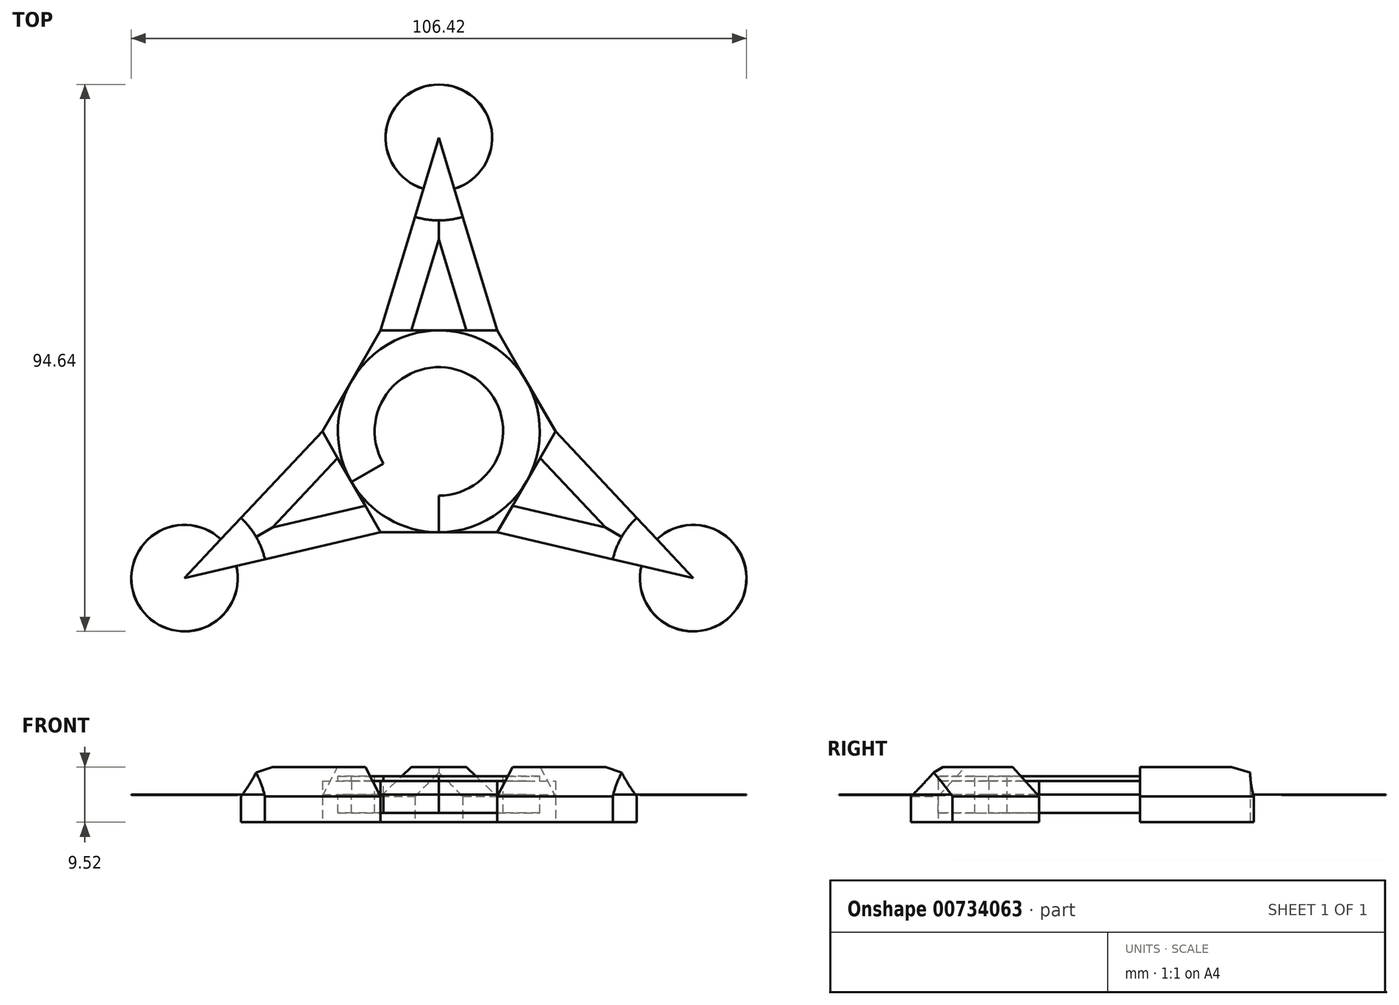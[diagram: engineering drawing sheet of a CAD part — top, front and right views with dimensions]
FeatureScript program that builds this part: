
annotation { "Feature Type Name" : "Feature", "Feature Type Description" : "" }
export const myFeature = defineFeature(function(context is Context, id is Id, definition is map)
    precondition{}
    {
        {
            var Q0;
            Q0=qCreatedBy(makeId("Top.planeOp"),FACE);
            var sketch = newSketch(context, id + "F0", { "sketchPlane" : qUnion([Q0])});
            skCircle(sketch, "E0", {"center": v(0, 0) * mm, "radius": 11.11 * mm});
            skCircle(sketch, "E1", {"center": v(0, 0) * mm, "radius": 17.46 * mm});
            skPoint(sketch, "E2.0.midPoint", {"position": v(15.12, 8.73) * mm});
            skCircle(sketch, "E3.cCircle", {"center": v(0, 0) * mm, "radius": 17.46 * mm, "construction": true});
            skLineSegment(sketch, "E3.0", {"start": v(10.08, 17.46) * mm, "end": v(20.16, 0) * mm});
            skLineSegment(sketch, "E3.1", {"start": v(20.16, 0) * mm, "end": v(10.08, -17.46) * mm});
            skLineSegment(sketch, "E3.2", {"start": v(10.08, -17.46) * mm, "end": v(-10.08, -17.46) * mm});
            skLineSegment(sketch, "E3.3", {"start": v(-10.08, -17.46) * mm, "end": v(-20.16, 0) * mm});
            skLineSegment(sketch, "E3.4", {"start": v(-20.16, 0) * mm, "end": v(-10.08, 17.46) * mm});
            skLineSegment(sketch, "E3.5", {"start": v(-10.08, 17.46) * mm, "end": v(10.08, 17.46) * mm});
            skLineSegment(sketch, "E4", {"start": v(-10.08, 17.46) * mm, "end": v(0, 50.8) * mm});
            skLineSegment(sketch, "E5", {"start": v(0, 50.8) * mm, "end": v(10.08, 17.46) * mm});
            skLineSegment(sketch, "E6", {"start": v(0, 50.8) * mm, "end": v(0, -50.8) * mm});
            skLineSegment(sketch, "E7", {"start": v(-20.16, 0) * mm, "end": v(-44, -25.4) * mm});
            skLineSegment(sketch, "E8", {"start": v(-44, -25.4) * mm, "end": v(-10.08, -17.46) * mm});
            skLineSegment(sketch, "E9", {"start": v(-44, -25.4) * mm, "end": v(44, 25.4) * mm});
            skLineSegment(sketch, "E10", {"start": v(10.08, -17.46) * mm, "end": v(44, -25.4) * mm});
            skLineSegment(sketch, "E11", {"start": v(44, -25.4) * mm, "end": v(20.16, 0) * mm});
            skLineSegment(sketch, "E12", {"start": v(44, -25.4) * mm, "end": v(-44, 25.4) * mm});
            skCircle(sketch, "E13", {"center": v(-44, -25.4) * mm, "radius": 14.29 * mm});
            skCircle(sketch, "E14", {"center": v(44, -25.4) * mm, "radius": 14.29 * mm});
            skCircle(sketch, "E15", {"center": v(0, 50.8) * mm, "radius": 14.29 * mm});
            skSolve(sketch);
        }
        {
            var Q0;
            {var subQ0=sQuery(id+"F0.wireOp",EDGE,"E9");var subQ1=sQuery(id+"F0.wireOp",EDGE,"E0");var subQ2=makeQuery(id+"F0.imprint","INTERSECT",VERTEX,{"disambiguationData":[OD(1.0)],"derivedFrom":[subQ1,subQ0]});Q0=makeQuery(id+"F0.imprint","IMPRINT",FACE,{"disambiguationData":[TD([[makeQuery(id+"F0.imprint","IMPRINT",EDGE,{"disambiguationData":[TD([[subQ2,-1.0]])],"derivedFrom":subQ1}),-1.0]])]});}
            var Q1;
            {var subQ0=sQuery(id+"F0.wireOp",EDGE,"E6");var subQ1=sQuery(id+"F0.wireOp",EDGE,"E0");var subQ2=makeQuery(id+"F0.imprint","INTERSECT",VERTEX,{"disambiguationData":[OD(0.0)],"derivedFrom":[subQ1,subQ0]});Q1=makeQuery(id+"F0.imprint","IMPRINT",FACE,{"disambiguationData":[TD([[makeQuery(id+"F0.imprint","IMPRINT",EDGE,{"disambiguationData":[TD([[subQ2,-1.0]])],"derivedFrom":subQ1}),-1.0]])]});}
            var Q2;
            {var subQ0=sQuery(id+"F0.wireOp",EDGE,"E12");var subQ1=sQuery(id+"F0.wireOp",EDGE,"E0");var subQ2=makeQuery(id+"F0.imprint","INTERSECT",VERTEX,{"disambiguationData":[OD(0.0)],"derivedFrom":[subQ1,subQ0]});Q2=makeQuery(id+"F0.imprint","IMPRINT",FACE,{"disambiguationData":[TD([[makeQuery(id+"F0.imprint","IMPRINT",EDGE,{"disambiguationData":[TD([[subQ2,-1.0]])],"derivedFrom":subQ1}),-1.0]])]});}
            var Q3;
            {var subQ0=sQuery(id+"F0.wireOp",EDGE,"E6");var subQ1=sQuery(id+"F0.wireOp",EDGE,"E0");var subQ2=makeQuery(id+"F0.imprint","INTERSECT",VERTEX,{"disambiguationData":[OD(0.0)],"derivedFrom":[subQ1,subQ0]});Q3=makeQuery(id+"F0.imprint","IMPRINT",FACE,{"disambiguationData":[TD([[makeQuery(id+"F0.imprint","IMPRINT",EDGE,{"disambiguationData":[TD([[subQ2,1.0]])],"derivedFrom":subQ1}),-1.0]])]});}
            var Q4;
            {var subQ0=sQuery(id+"F0.wireOp",EDGE,"E9");var subQ1=sQuery(id+"F0.wireOp",EDGE,"E0");var subQ2=makeQuery(id+"F0.imprint","INTERSECT",VERTEX,{"disambiguationData":[OD(0.0)],"derivedFrom":[subQ1,subQ0]});Q4=makeQuery(id+"F0.imprint","IMPRINT",FACE,{"disambiguationData":[TD([[makeQuery(id+"F0.imprint","IMPRINT",EDGE,{"disambiguationData":[TD([[subQ2,1.0]])],"derivedFrom":subQ1}),-1.0]])]});}
            var Q5;
            {var subQ0=sQuery(id+"F0.wireOp",EDGE,"E6");var subQ1=sQuery(id+"F0.wireOp",EDGE,"E0");var subQ2=makeQuery(id+"F0.imprint","INTERSECT",VERTEX,{"disambiguationData":[OD(1.0)],"derivedFrom":[subQ1,subQ0]});Q5=makeQuery(id+"F0.imprint","IMPRINT",FACE,{"disambiguationData":[TD([[makeQuery(id+"F0.imprint","IMPRINT",EDGE,{"disambiguationData":[TD([[subQ2,-1.0]])],"derivedFrom":subQ1}),-1.0]])]});}
            extrude(context, id + "F1", {"entities" : qUnion([Q0, Q1, Q2, Q3, Q4, Q5]), "oppositeDirection" : true, "depth" : 3.17 * mm, "offsetDistance" : 25.4 * mm, "hasSecondDirection" : true, "secondDirectionOppositeDirection" : false, "secondDirectionDepth" : 3.17 * mm});
        }
        {
            var Q0;
            {var subQ0=sQuery(id+"F0.wireOp",EDGE,"E3.4");var subQ1=sQuery(id+"F0.wireOp",EDGE,"E1");var subQ2=makeQuery(id+"F0.imprint","INTERSECT",VERTEX,{"derivedFrom":[subQ1,subQ0,sQuery(id+"F0.wireOp",EDGE,"E12")]});Q0=makeQuery(id+"F0.imprint","IMPRINT",FACE,{"disambiguationData":[TD([[makeQuery(id+"F0.imprint","IMPRINT",EDGE,{"disambiguationData":[TD([[subQ2,-1.0]])],"derivedFrom":subQ1}),-1.0]])]});}
            var Q1;
            {var subQ0=sQuery(id+"F0.wireOp",EDGE,"E3.2");var subQ1=sQuery(id+"F0.wireOp",EDGE,"E1");var subQ2=makeQuery(id+"F0.imprint","INTERSECT",VERTEX,{"derivedFrom":[subQ1,subQ0,sQuery(id+"F0.wireOp",EDGE,"E6")]});Q1=makeQuery(id+"F0.imprint","IMPRINT",FACE,{"disambiguationData":[TD([[makeQuery(id+"F0.imprint","IMPRINT",EDGE,{"disambiguationData":[TD([[subQ2,1.0]])],"derivedFrom":subQ1}),-1.0]])]});}
            var Q2;
            {var subQ0=sQuery(id+"F0.wireOp",EDGE,"E3.4");var subQ1=sQuery(id+"F0.wireOp",EDGE,"E1");var subQ2=makeQuery(id+"F0.imprint","INTERSECT",VERTEX,{"derivedFrom":[subQ1,subQ0,sQuery(id+"F0.wireOp",EDGE,"E12")]});Q2=makeQuery(id+"F0.imprint","IMPRINT",FACE,{"disambiguationData":[TD([[makeQuery(id+"F0.imprint","IMPRINT",EDGE,{"disambiguationData":[TD([[subQ2,1.0]])],"derivedFrom":subQ1}),-1.0]])]});}
            var Q3;
            {var subQ0=sQuery(id+"F0.wireOp",EDGE,"E3.0");var subQ1=sQuery(id+"F0.wireOp",EDGE,"E1");var subQ2=makeQuery(id+"F0.imprint","INTERSECT",VERTEX,{"derivedFrom":[subQ1,subQ0,sQuery(id+"F0.wireOp",EDGE,"E9")]});Q3=makeQuery(id+"F0.imprint","IMPRINT",FACE,{"disambiguationData":[TD([[makeQuery(id+"F0.imprint","IMPRINT",EDGE,{"disambiguationData":[TD([[subQ2,-1.0]])],"derivedFrom":subQ1}),-1.0]])]});}
            var Q4;
            {var subQ0=sQuery(id+"F0.wireOp",EDGE,"E3.2");var subQ1=sQuery(id+"F0.wireOp",EDGE,"E1");var subQ2=makeQuery(id+"F0.imprint","INTERSECT",VERTEX,{"derivedFrom":[subQ1,subQ0,sQuery(id+"F0.wireOp",EDGE,"E6")]});Q4=makeQuery(id+"F0.imprint","IMPRINT",FACE,{"disambiguationData":[TD([[makeQuery(id+"F0.imprint","IMPRINT",EDGE,{"disambiguationData":[TD([[subQ2,-1.0]])],"derivedFrom":subQ1}),-1.0]])]});}
            var Q5;
            {var subQ0=sQuery(id+"F0.wireOp",EDGE,"E3.0");var subQ1=sQuery(id+"F0.wireOp",EDGE,"E1");var subQ2=makeQuery(id+"F0.imprint","INTERSECT",VERTEX,{"derivedFrom":[subQ1,subQ0,sQuery(id+"F0.wireOp",EDGE,"E9")]});Q5=makeQuery(id+"F0.imprint","IMPRINT",FACE,{"disambiguationData":[TD([[makeQuery(id+"F0.imprint","IMPRINT",EDGE,{"disambiguationData":[TD([[subQ2,1.0]])],"derivedFrom":subQ1}),-1.0]])]});}
            extrude(context, id + "F2", {"entities" : qUnion([Q0, Q1, Q2, Q3, Q4, Q5]), "operationType" : NewBodyOperationType.ADD, "depth" : 2.38 * mm, "offsetDistance" : 25.4 * mm, "hasSecondDirection" : true, "secondDirectionOppositeDirection" : true, "secondDirectionDepth" : 3 / 812.8 * mm});
        }
        {
            var Q0;
            {var subQ0=sQuery(id+"F0.wireOp",EDGE,"E10");var subQ5=sQuery(id+"F0.wireOp",EDGE,"E14");var subQ6=makeQuery(id+"F0.imprint","INTERSECT",VERTEX,{"derivedFrom":[subQ0,subQ5]});Q0=makeQuery(id+"F0.imprint","IMPRINT",FACE,{"disambiguationData":[TD([[makeQuery(id+"F0.imprint","IMPRINT",EDGE,{"disambiguationData":[TD([[subQ6,1.0]])],"derivedFrom":subQ5}),-1.0]])]});}
            var Q1;
            {var subQ0=sQuery(id+"F0.wireOp",EDGE,"E11");var subQ5=sQuery(id+"F0.wireOp",EDGE,"E14");var subQ7=makeQuery(id+"F0.imprint","INTERSECT",VERTEX,{"derivedFrom":[subQ0,subQ5]});Q1=makeQuery(id+"F0.imprint","IMPRINT",FACE,{"disambiguationData":[TD([[makeQuery(id+"F0.imprint","IMPRINT",EDGE,{"disambiguationData":[TD([[subQ7,-1.0]])],"derivedFrom":subQ5}),-1.0]])]});}
            var Q2;
            {var subQ0=sQuery(id+"F0.wireOp",EDGE,"E5");var subQ5=sQuery(id+"F0.wireOp",EDGE,"E15");var subQ6=makeQuery(id+"F0.imprint","INTERSECT",VERTEX,{"derivedFrom":[subQ0,subQ5]});Q2=makeQuery(id+"F0.imprint","IMPRINT",FACE,{"disambiguationData":[TD([[makeQuery(id+"F0.imprint","IMPRINT",EDGE,{"disambiguationData":[TD([[subQ6,1.0]])],"derivedFrom":subQ5}),-1.0]])]});}
            var Q3;
            {var subQ0=sQuery(id+"F0.wireOp",EDGE,"E4");var subQ5=sQuery(id+"F0.wireOp",EDGE,"E15");var subQ6=makeQuery(id+"F0.imprint","INTERSECT",VERTEX,{"derivedFrom":[subQ0,subQ5]});Q3=makeQuery(id+"F0.imprint","IMPRINT",FACE,{"disambiguationData":[TD([[makeQuery(id+"F0.imprint","IMPRINT",EDGE,{"disambiguationData":[TD([[subQ6,-1.0]])],"derivedFrom":subQ5}),-1.0]])]});}
            var Q4;
            {var subQ0=sQuery(id+"F0.wireOp",EDGE,"E8");var subQ5=sQuery(id+"F0.wireOp",EDGE,"E13");var subQ6=makeQuery(id+"F0.imprint","INTERSECT",VERTEX,{"derivedFrom":[subQ0,subQ5]});Q4=makeQuery(id+"F0.imprint","IMPRINT",FACE,{"disambiguationData":[TD([[makeQuery(id+"F0.imprint","IMPRINT",EDGE,{"disambiguationData":[TD([[subQ6,-1.0]])],"derivedFrom":subQ5}),-1.0]])]});}
            var Q5;
            {var subQ0=sQuery(id+"F0.wireOp",EDGE,"E7");var subQ5=sQuery(id+"F0.wireOp",EDGE,"E13");var subQ6=makeQuery(id+"F0.imprint","INTERSECT",VERTEX,{"derivedFrom":[subQ0,subQ5]});Q5=makeQuery(id+"F0.imprint","IMPRINT",FACE,{"disambiguationData":[TD([[makeQuery(id+"F0.imprint","IMPRINT",EDGE,{"disambiguationData":[TD([[subQ6,1.0]])],"derivedFrom":subQ5}),-1.0]])]});}
            extrude(context, id + "F3", {"entities" : qUnion([Q0, Q1, Q2, Q3, Q4, Q5]), "surfaceOperationType" : NewSurfaceOperationType.ADD, "depth" : 4.76 * mm, "offsetDistance" : 25.4 * mm, "hasSecondDirection" : true, "secondDirectionOppositeDirection" : true, "secondDirectionDepth" : 4.76 * mm});
        }
        {
            var Q0;
            {var subQ1=sQuery(id+"F0.wireOp",EDGE,"E4");var subQ3=sQuery(id+"F0.wireOp",EDGE,"E15");var subQ4=makeQuery(id+"F0.imprint","INTERSECT",VERTEX,{"derivedFrom":[subQ1,subQ3]});Q0=makeQuery(id+"F0.imprint","IMPRINT",FACE,{"disambiguationData":[TD([[makeQuery(id+"F0.imprint","IMPRINT",EDGE,{"disambiguationData":[TD([[subQ4,1.0]])],"derivedFrom":subQ3}),1.0]])]});}
            var Q1;
            {var subQ1=sQuery(id+"F0.wireOp",EDGE,"E7");var subQ3=sQuery(id+"F0.wireOp",EDGE,"E13");var subQ4=makeQuery(id+"F0.imprint","INTERSECT",VERTEX,{"derivedFrom":[subQ1,subQ3]});Q1=makeQuery(id+"F0.imprint","IMPRINT",FACE,{"disambiguationData":[TD([[makeQuery(id+"F0.imprint","IMPRINT",EDGE,{"disambiguationData":[TD([[subQ4,-1.0]])],"derivedFrom":subQ3}),1.0]])]});}
            var Q2;
            {var subQ1=sQuery(id+"F0.wireOp",EDGE,"E10");var subQ3=sQuery(id+"F0.wireOp",EDGE,"E14");var subQ4=makeQuery(id+"F0.imprint","INTERSECT",VERTEX,{"derivedFrom":[subQ1,subQ3]});Q2=makeQuery(id+"F0.imprint","IMPRINT",FACE,{"disambiguationData":[TD([[makeQuery(id+"F0.imprint","IMPRINT",EDGE,{"disambiguationData":[TD([[subQ4,-1.0]])],"derivedFrom":subQ3}),1.0]])]});}
            extrude(context, id + "F4", {"entities" : qUnion([Q0, Q1, Q2]), "depth" : 5 / 812.8 * mm, "offsetDistance" : 25.4 * mm, "hasSecondDirection" : true, "secondDirectionOppositeDirection" : true, "secondDirectionDepth" : 5 / 812.8 * mm});
        }
        {
            var Q0;
            {var subQ1=sQuery(id+"F0.wireOp",EDGE,"E10");var subQ3=sQuery(id+"F0.wireOp",EDGE,"E14");var subQ4=makeQuery(id+"F0.imprint","INTERSECT",VERTEX,{"derivedFrom":[subQ1,subQ3]});Q0=makeQuery(id+"F0.imprint","IMPRINT",FACE,{"disambiguationData":[TD([[makeQuery(id+"F0.imprint","IMPRINT",EDGE,{"disambiguationData":[TD([[subQ4,1.0]])],"derivedFrom":subQ3}),1.0]])]});}
            var Q1;
            {var subQ1=sQuery(id+"F0.wireOp",EDGE,"E11");var subQ3=sQuery(id+"F0.wireOp",EDGE,"E14");var subQ4=makeQuery(id+"F0.imprint","INTERSECT",VERTEX,{"derivedFrom":[subQ1,subQ3]});Q1=makeQuery(id+"F0.imprint","IMPRINT",FACE,{"disambiguationData":[TD([[makeQuery(id+"F0.imprint","IMPRINT",EDGE,{"disambiguationData":[TD([[subQ4,-1.0]])],"derivedFrom":subQ3}),1.0]])]});}
            var Q2;
            {var subQ1=sQuery(id+"F0.wireOp",EDGE,"E5");var subQ3=sQuery(id+"F0.wireOp",EDGE,"E15");var subQ4=makeQuery(id+"F0.imprint","INTERSECT",VERTEX,{"derivedFrom":[subQ1,subQ3]});Q2=makeQuery(id+"F0.imprint","IMPRINT",FACE,{"disambiguationData":[TD([[makeQuery(id+"F0.imprint","IMPRINT",EDGE,{"disambiguationData":[TD([[subQ4,1.0]])],"derivedFrom":subQ3}),1.0]])]});}
            var Q3;
            {var subQ1=sQuery(id+"F0.wireOp",EDGE,"E4");var subQ3=sQuery(id+"F0.wireOp",EDGE,"E15");var subQ4=makeQuery(id+"F0.imprint","INTERSECT",VERTEX,{"derivedFrom":[subQ1,subQ3]});Q3=makeQuery(id+"F0.imprint","IMPRINT",FACE,{"disambiguationData":[TD([[makeQuery(id+"F0.imprint","IMPRINT",EDGE,{"disambiguationData":[TD([[subQ4,-1.0]])],"derivedFrom":subQ3}),1.0]])]});}
            var Q4;
            {var subQ1=sQuery(id+"F0.wireOp",EDGE,"E7");var subQ3=sQuery(id+"F0.wireOp",EDGE,"E13");var subQ4=makeQuery(id+"F0.imprint","INTERSECT",VERTEX,{"derivedFrom":[subQ1,subQ3]});Q4=makeQuery(id+"F0.imprint","IMPRINT",FACE,{"disambiguationData":[TD([[makeQuery(id+"F0.imprint","IMPRINT",EDGE,{"disambiguationData":[TD([[subQ4,1.0]])],"derivedFrom":subQ3}),1.0]])]});}
            var Q5;
            {var subQ1=sQuery(id+"F0.wireOp",EDGE,"E8");var subQ3=sQuery(id+"F0.wireOp",EDGE,"E13");var subQ4=makeQuery(id+"F0.imprint","INTERSECT",VERTEX,{"derivedFrom":[subQ1,subQ3]});Q5=makeQuery(id+"F0.imprint","IMPRINT",FACE,{"disambiguationData":[TD([[makeQuery(id+"F0.imprint","IMPRINT",EDGE,{"disambiguationData":[TD([[subQ4,-1.0]])],"derivedFrom":subQ3}),1.0]])]});}
            extrude(context, id + "F5", {"entities" : qUnion([Q0, Q1, Q2, Q3, Q4, Q5]), "depth" : 3 / 812.8 * mm, "offsetDistance" : 25.4 * mm, "hasSecondDirection" : true, "secondDirectionOppositeDirection" : true, "secondDirectionDepth" : 3 / 812.8 * mm});
        }
        {
            var Q0;
            Q0=makeQuery(id+"F3.opExtrude","CAP_EDGE",EDGE,{"disambiguationData":[OSD([sQuery(id+"F0.wireOp",EDGE,"E8")])],"isStart":false});
            var Q1;
            Q1=makeQuery(id+"F3.opExtrude","CAP_EDGE",EDGE,{"disambiguationData":[OSD([sQuery(id+"F0.wireOp",EDGE,"E7")])],"isStart":false});
            var Q2;
            Q2=makeQuery(id+"F3.opExtrude","CAP_EDGE",EDGE,{"disambiguationData":[OSD([sQuery(id+"F0.wireOp",EDGE,"E10")])],"isStart":false});
            var Q3;
            Q3=makeQuery(id+"F3.opExtrude","CAP_EDGE",EDGE,{"disambiguationData":[OSD([sQuery(id+"F0.wireOp",EDGE,"E11")])],"isStart":false});
            var Q4;
            Q4=makeQuery(id+"F3.opExtrude","CAP_EDGE",EDGE,{"disambiguationData":[OSD([sQuery(id+"F0.wireOp",EDGE,"E5")])],"isStart":false});
            var Q5;
            Q5=makeQuery(id+"F3.opExtrude","CAP_EDGE",EDGE,{"disambiguationData":[OSD([sQuery(id+"F0.wireOp",EDGE,"E4")])],"isStart":false});
            var Q6;
            Q6=makeQuery(id+"F4.opExtrude","CAP_EDGE",EDGE,{"disambiguationData":[OSD([sQuery(id+"F0.wireOp",EDGE,"E15")])],"isStart":false});
            var Q7;
            Q7=makeQuery(id+"F4.opExtrude","CAP_EDGE",EDGE,{"disambiguationData":[OSD([sQuery(id+"F0.wireOp",EDGE,"E14")])],"isStart":false});
            var Q8;
            Q8=makeQuery(id+"F4.opExtrude","CAP_EDGE",EDGE,{"disambiguationData":[OSD([sQuery(id+"F0.wireOp",EDGE,"E13")])],"isStart":false});
            chamfer(context, id + "F6", {"entities" : qUnion([Q0, Q1, Q2, Q3, Q4, Q5, Q6, Q7, Q8]), "width" : 5.08 * mm, "tangentPropagation" : true});
        }
    });
